# Revit family: 6220_Eisenrohranschluß flachdichtend (4037,7762,7763,7760)
name_source: partatom
category: Rohrformteile
units: mm (PartAtom-declared; Revit-internal decimal feet)

## family parameters
Arbeitsebenenbasiert = Nein
Beim Laden mit Abzugskörper schneiden = Nein
Bemaßung runder Anschluss = Durchmesser verwenden
Gemeinsam genutzt = Nein
Immer vertikal = Ja
OmniClass-Nummer = 23.65.55.14
OmniClass-Titel = Valves for Liquid Services
Teiletyp = Verbindung

## types (8) — shared parameters
Ausführung = Eisenrohranschluss flachdichtend, Mutter und Anschlussstück.
Flachdichtung = Klinger SIL- C4400
Hersteller = HERZ Armaturen Ges.m.b.H.
Max. Betriebsdruck = 1000000.0 Pa
Max. Betriebstemperatur = 110 °C
Medium = Heizungswasser nach ÖNORM H5195 oder VDI- Richtlinie 2035.
Die Verwendung von Ethylen- oder Propyleneglykol in einem Mischungsverhältnis 25- 50% ist zulässig.
Mutter = Messing CW614N, vernickelt
S02 = 8 mm  [stored 0.0262467 ft]
SCRNCODE = 07;01;02
SCRNSEQ = AWI;AWI_TYP="1001";2
URL = www.herz-armaturen.at
Verschraubung = Messing CW614N, vernickelt
zero-valued in all types: Vorgabe-Ansicht

## per-type parameters (varying)
| type | 11_4x2 | 1_2x3_8 | 1x3_4 | 2x5_4 | 3_2x5_4 | 3_4x1_2 | 5_8x3_8 | 9_4x3_2 | Bestellnummer |
| G5/8 x R3/8 | Nein | Nein | Nein | Nein | Nein | Nein | Ja | Nein | 1622000 |
| G1/2 x R3/8 | Nein | Ja | Nein | Nein | Nein | Nein | Nein | Nein | 1622020 |
| G3/4 x R1/2 | Nein | Nein | Nein | Nein | Nein | Ja | Nein | Nein | 1622021 |
| G1 x R3/4 | Nein | Nein | Ja | Nein | Nein | Nein | Nein | Nein | 1622012 |
| G1 1/2 x R1 1/4 | Nein | Nein | Nein | Nein | Ja | Nein | Nein | Nein | 1622064 |
| G2 x R1 1/4 | Nein | Nein | Nein | Ja | Nein | Nein | Nein | Nein | 1622074 |
| G2 1/4 x R1 1/2 | Nein | Nein | Nein | Nein | Nein | Nein | Nein | Ja | 1622075 |
| G2 3/4 x R2 | Ja | Nein | Nein | Nein | Nein | Nein | Nein | Nein | 1622076 |

note: [stored X ft] marks values corroborated as IEEE doubles in the binary element streams (Revit-internal decimal feet)
